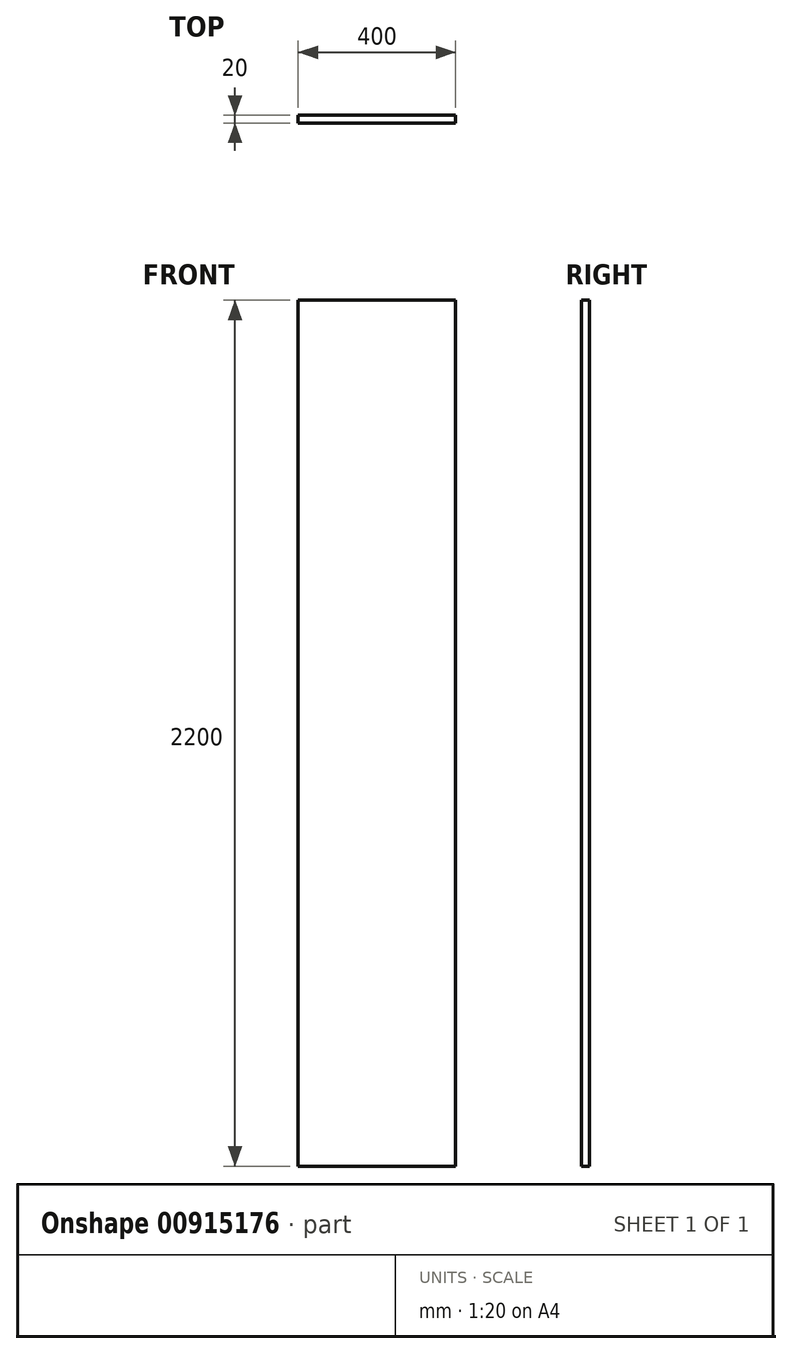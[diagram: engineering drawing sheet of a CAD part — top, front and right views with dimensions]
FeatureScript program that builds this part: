
annotation { "Feature Type Name" : "Feature", "Feature Type Description" : "" }
export const myFeature = defineFeature(function(context is Context, id is Id, definition is map)
    precondition{}
    {
        {
            var Q0;
            Q0=qCreatedBy(makeId("Front.planeOp"),FACE);
            var sketch = newSketch(context, id + "F0", { "sketchPlane" : qUnion([Q0])});
            skLineSegment(sketch, "E0", {"start": v(0, 0) * mm, "end": v(400, 0) * mm});
            skLineSegment(sketch, "E1", {"start": v(400, 0) * mm, "end": v(400, 2200) * mm});
            skLineSegment(sketch, "E2", {"start": v(400, 2200) * mm, "end": v(0, 2200) * mm});
            skLineSegment(sketch, "E3", {"start": v(0, 2200) * mm, "end": v(0, 0) * mm});
            skSolve(sketch);
        }
        {
            var Q0;
            Q0 = qSketchRegion(id + "F0", true);
            extrude(context, id + "F1", {"entities" : qUnion([Q0]), "depth" : 20 * mm, "offsetDistance" : 25 * mm});
        }
    });
